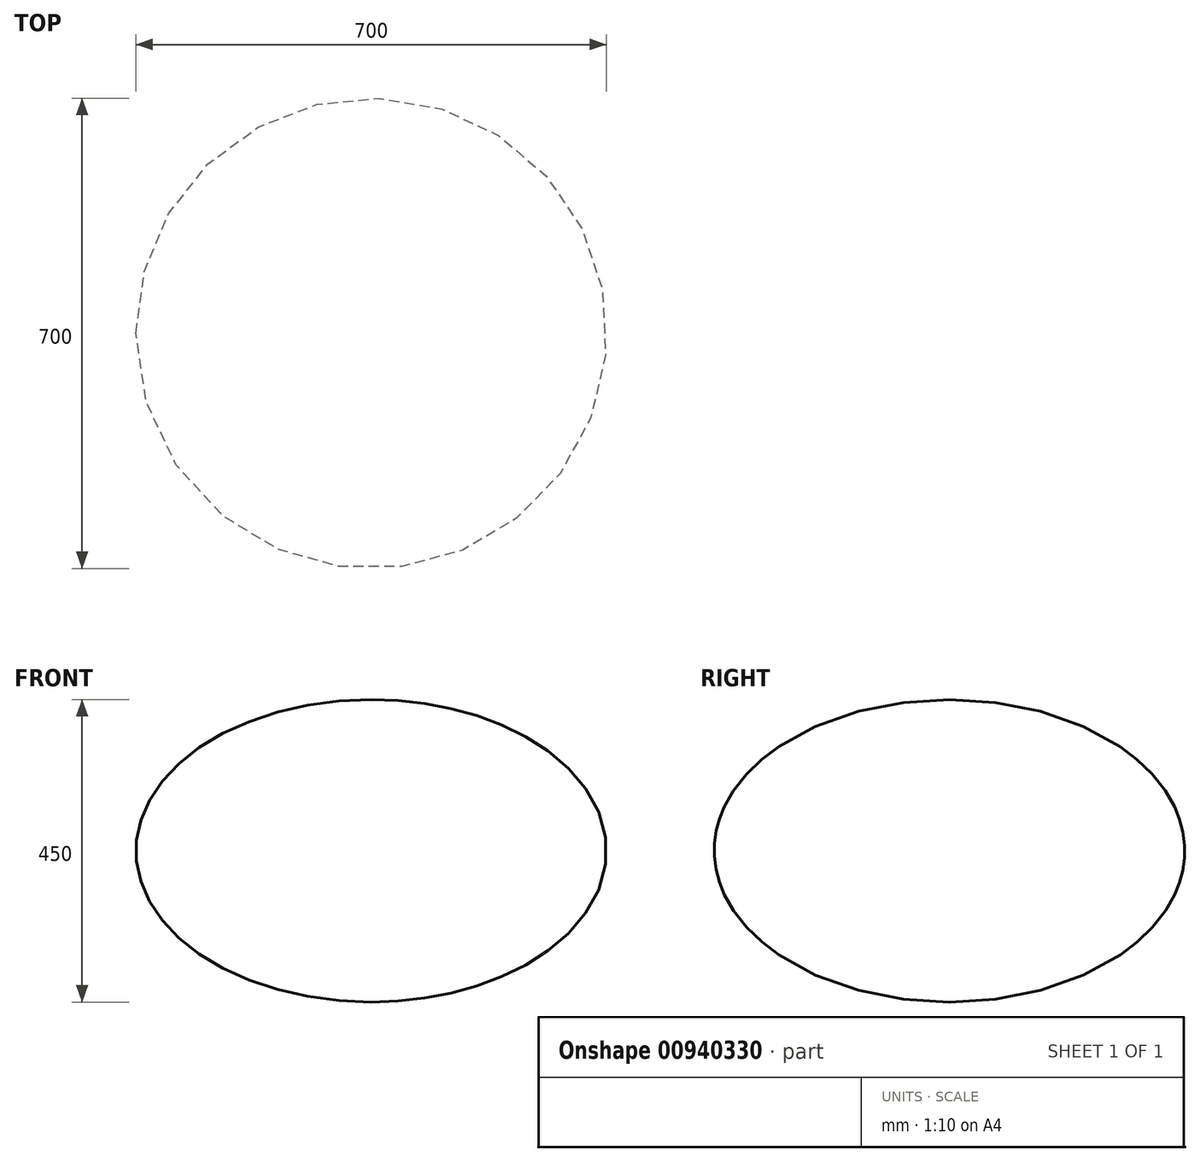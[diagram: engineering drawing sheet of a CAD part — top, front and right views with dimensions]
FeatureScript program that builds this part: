
annotation { "Feature Type Name" : "Feature", "Feature Type Description" : "" }
export const myFeature = defineFeature(function(context is Context, id is Id, definition is map)
    precondition{}
    {
        {
            var Q0;
            Q0=qCreatedBy(makeId("Front.planeOp"),FACE);
            var sketch = newSketch(context, id + "F0", { "sketchPlane" : qUnion([Q0])});
            skEllipticalArc(sketch, "E0", {});
            skLineSegment(sketch, "E1", {"start": v(0, 225) * mm, "end": v(0, -225) * mm});
            const initialGuessF0  = {"E0": [0, 0, -1, 0, 0.35, 0.225, 4.71238898038469, 1.5707963267948966]};
            skSetInitialGuess(sketch, initialGuessF0);
            skSolve(sketch);
        }
        {
            var Q0;
            Q0=makeQuery(id+"F0.imprint","IMPRINT",FACE,{"disambiguationData":[TD([[makeQuery(id+"F0.imprint","IMPRINT",EDGE,{"derivedFrom":sQuery(id+"F0.wireOp",EDGE,"E0")}),1.0]])]});
            var Q1;
            Q1=sQuery(id+"F0.wireOp",EDGE,"E1");
            revolve(context, id + "F1", {"surfaceOperationType" : NewSurfaceOperationType.NEW, "entities" : qUnion([Q0]), "axis" : qUnion([Q1]), "revolveType" : RevolveType.FULL});
        }
    });
